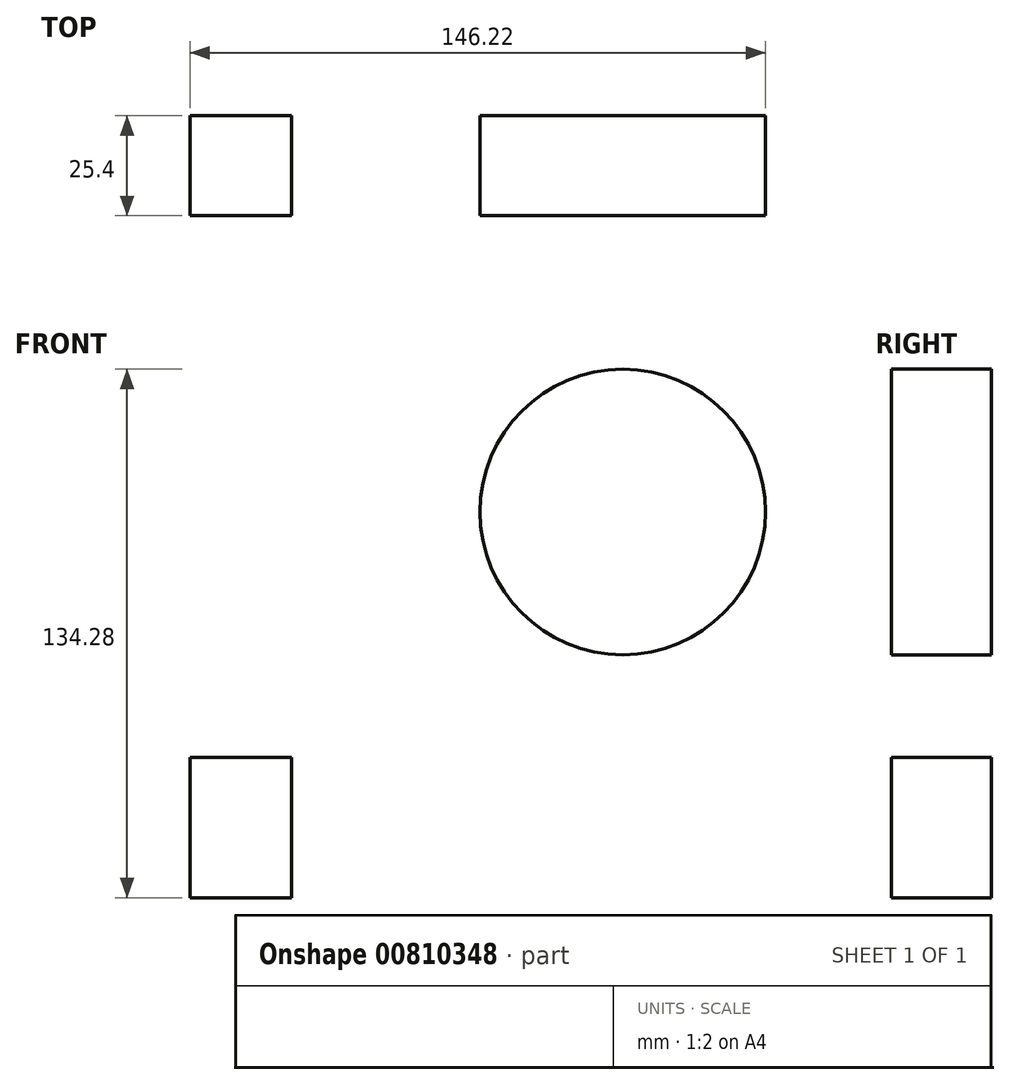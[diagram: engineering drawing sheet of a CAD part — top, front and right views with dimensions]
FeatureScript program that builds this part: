
annotation { "Feature Type Name" : "Feature", "Feature Type Description" : "" }
export const myFeature = defineFeature(function(context is Context, id is Id, definition is map)
    precondition{}
    {
        {
            var Q0;
            Q0=qCreatedBy(makeId("Front.planeOp"),FACE);
            var sketch = newSketch(context, id + "F0", { "sketchPlane" : qUnion([Q0])});
            skLineSegment(sketch, "E0.bottom", {"start": v(-151.77, 6.9) * mm, "end": v(-125.97, 6.9) * mm});
            skLineSegment(sketch, "E0.top", {"start": v(-151.77, -28.77) * mm, "end": v(-125.97, -28.77) * mm});
            skLineSegment(sketch, "E0.left", {"start": v(-151.77, 6.9) * mm, "end": v(-151.77, -28.77) * mm});
            skLineSegment(sketch, "E0.right", {"start": v(-125.97, 6.9) * mm, "end": v(-125.97, -28.77) * mm});
            skSolve(sketch);
        }
        {
            var Q0;
            Q0=qSketchRegion(id+"F0",true);
            extrude(context, id + "F1", {"entities" : qUnion([Q0]), "depth" : 25.4 * mm, "offsetDistance" : 25.4 * mm});
        }
        {
            var Q0;
            Q0=qCreatedBy(makeId("Front.planeOp"),FACE);
            var sketch = newSketch(context, id + "F2", { "sketchPlane" : qUnion([Q0])});
            skCircle(sketch, "E1", {"center": v(-41.82, 69.24) * mm, "radius": 36.27 * mm});
            skSolve(sketch);
        }
        {
            var Q0;
            Q0 = qSketchRegion(id + "F2", true);
            extrude(context, id + "F3", {"entities" : qUnion([Q0]), "depth" : 25.4 * mm, "offsetDistance" : 25.4 * mm});
        }
    });
